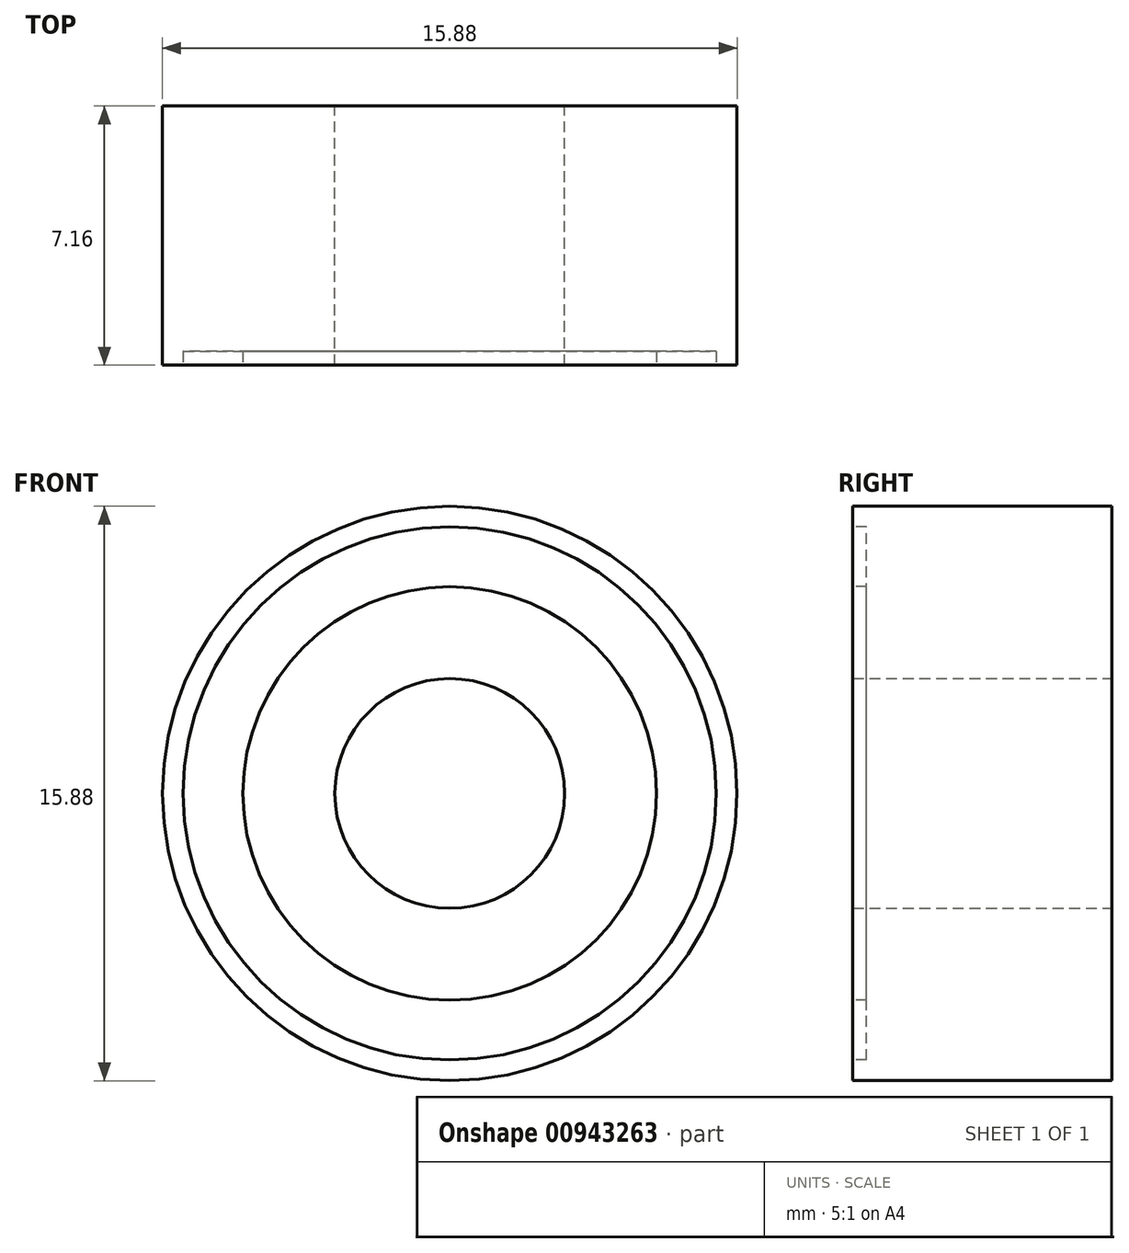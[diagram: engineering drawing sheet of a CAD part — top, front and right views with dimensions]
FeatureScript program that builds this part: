
annotation { "Feature Type Name" : "Feature", "Feature Type Description" : "" }
export const myFeature = defineFeature(function(context is Context, id is Id, definition is map)
    precondition{}
    {
        {
            var Q0;
            Q0=qCreatedBy(makeId("Front.planeOp"),FACE);
            var sketch = newSketch(context, id + "F0", { "sketchPlane" : qUnion([Q0])});
            skCircle(sketch, "E0", {"center": v(0, 0) * mm, "radius": 7.94 * mm});
            skCircle(sketch, "E1", {"center": v(0, 0) * mm, "radius": 5.08 * mm});
            skSolve(sketch);
        }
        {
            var Q0;
            Q0=qSketchRegion(id+"F0",true);
            extrude(context, id + "F1", {"entities" : qUnion([Q0]), "endBound" : BoundingType.SYMMETRIC, "depth" : 7.16 * mm, "offsetDistance" : 25.4 * mm});
        }
        {
            var Q0;
            Q0=makeQuery(id+"F1.opExtrude","CAP_FACE",FACE,{"disambiguationData":[OSD([sQuery(id+"F0.wireOp",EDGE,"E0"),sQuery(id+"F0.wireOp",EDGE,"E1")])],"isStart":false});
            var sketch = newSketch(context, id + "F2", { "sketchPlane" : qUnion([Q0])});
            skCircle(sketch, "E2", {"center": v(0, 0) * mm, "radius": 5.72 * mm});
            skCircle(sketch, "E3", {"center": v(0, 0) * mm, "radius": 7.37 * mm});
            skSolve(sketch);
        }
        {
            var Q0;
            Q0=qSketchRegion(id+"F2",true);
            extrude(context, id + "F3", {"entities" : qUnion([Q0]), "operationType" : NewBodyOperationType.REMOVE, "oppositeDirection" : true, "depth" : 0.38 * mm, "offsetDistance" : 25.4 * mm});
        }
        {
            var Q0;
            Q0=qCreatedBy(makeId("Front.planeOp"),FACE);
            var sketch = newSketch(context, id + "F4", { "sketchPlane" : qUnion([Q0])});
            skCircle(sketch, "E4", {"center": v(0, 0) * mm, "radius": 5.08 * mm});
            skCircle(sketch, "E5", {"center": v(0, 0) * mm, "radius": 3.18 * mm});
            skSolve(sketch);
        }
        {
            var Q0;
            Q0 = qSketchRegion(id + "F4", true);
            var Q1;
            Q1=sQuery(id+"F4.wireOp",EDGE,"E4");
            var Q2;
            Q2=sQuery(id+"F4.wireOp",EDGE,"E5");
            extrude(context, id + "F5", {"entities" : qUnion([Q0]), "operationType" : NewBodyOperationType.ADD, "surfaceEntities" : qUnion([Q1, Q2]), "endBound" : BoundingType.SYMMETRIC, "depth" : 7.16 * mm, "offsetDistance" : 25.4 * mm});
        }
    });
